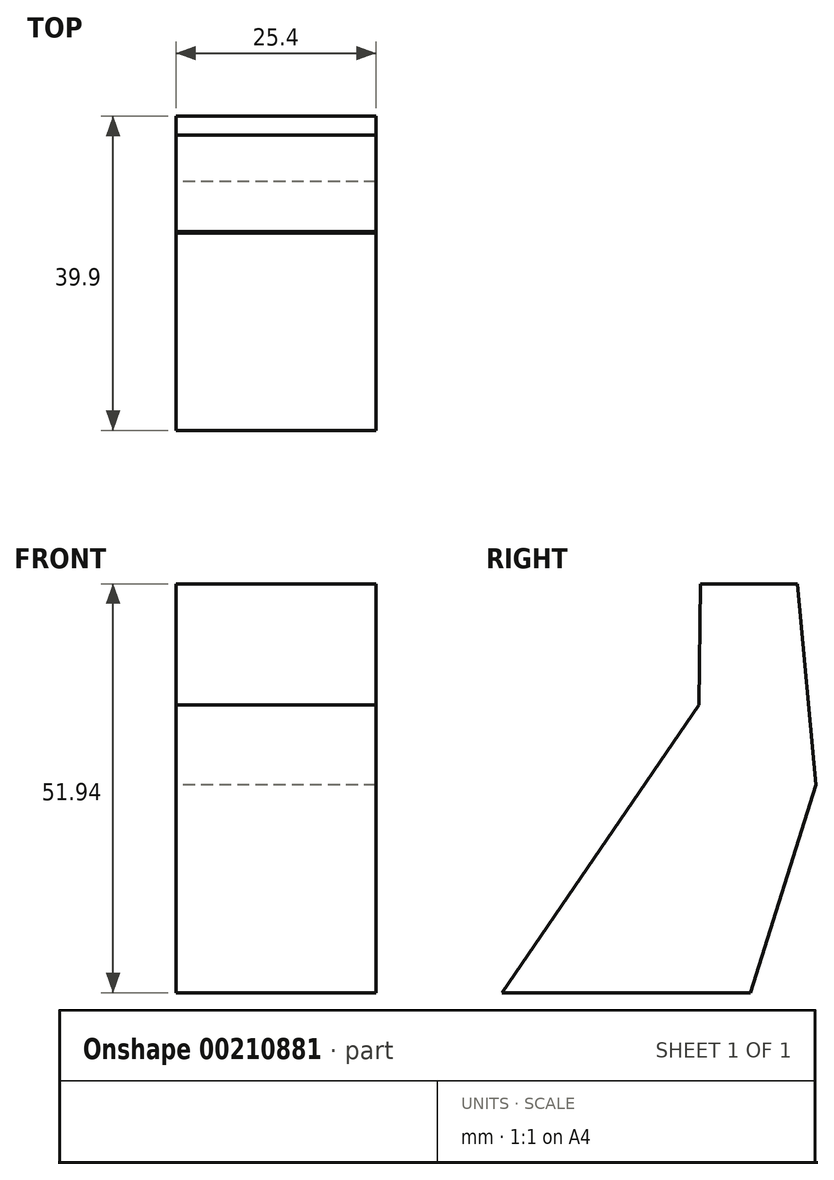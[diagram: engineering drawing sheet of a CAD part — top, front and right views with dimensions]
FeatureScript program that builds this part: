
annotation { "Feature Type Name" : "Feature", "Feature Type Description" : "" }
export const myFeature = defineFeature(function(context is Context, id is Id, definition is map)
    precondition{}
    {
        {
            var Q0;
            Q0=qCreatedBy(makeId("Right.planeOp"),FACE);
            var sketch = newSketch(context, id + "F0", { "sketchPlane" : qUnion([Q0])});
            skLineSegment(sketch, "E0", {"start": v(56.89, 54.53) * mm, "end": v(44.62, 54.53) * mm});
            skLineSegment(sketch, "E1", {"start": v(44.62, 54.53) * mm, "end": v(44.43, 39.14) * mm});
            skLineSegment(sketch, "E2", {"start": v(44.43, 39.14) * mm, "end": v(19.39, 2.6) * mm});
            skLineSegment(sketch, "E3", {"start": v(19.39, 2.6) * mm, "end": v(50.96, 2.6) * mm});
            skLineSegment(sketch, "E4", {"start": v(50.96, 2.6) * mm, "end": v(59.3, 29) * mm});
            skLineSegment(sketch, "E5", {"start": v(59.3, 29) * mm, "end": v(56.89, 54.53) * mm});
            skSolve(sketch);
        }
        {
            var Q0;
            Q0=makeQuery(id+"F0.imprint","IMPRINT",FACE,{"disambiguationData":[TD([[makeQuery(id+"F0.imprint","IMPRINT",EDGE,{"derivedFrom":sQuery(id+"F0.wireOp",EDGE,"E0")}),1.0]])]});
            var Q1;
            Q1=sQuery(id+"F0.wireOp",EDGE,"E2");
            extrude(context, id + "F2", {"entities" : qUnion([Q0]), "surfaceEntities" : qUnion([Q1]), "depth" : 25.4 * mm});
        }
    });
